# Revit family: NBS_AndersonGECLtd_ShlfUnits_V90ShelvingSystem
name_source: partatom
category: Furniture
revit_build: Autodesk Revit 2017 (Build: 20160225_1515(x64)
units: mm (PartAtom-declared; Revit-internal decimal feet)

## family parameters
Cut with Voids When Loaded = No
Host = Face
Room Calculation Point = No
Shared = No

## types (28) — shared parameters
AssetType = Fixed
Brackets = 170, 270, 370, 470, 570 mm
Category = Pr_40_30_78_77:Shelf units
Default Elevation = 1000 mm  [stored 3.28084 ft]
Description = A wall-fixed 3-part stainless steel system
DimensionsShelfSpacing = 400, 600, 800, 1000, 1500, 1800, 2000 mm
DurationUnit = year
ExpectedLife = 30 years
Features = Components available individually can can be configured as required, shelves , are solid, components can be used in combination with other materials
Finish = Brushed satin stainless steel
Form = Wall mounted single sided unit
IfcExportAs = IfcFurnitureType
IfcExportType = SHELVING
IntegralAccessories = Perforated shelves, barred shelf
IsBuiltIn = Yes
IsMultipleShelves = Yes
IsSingleShelf = No
ManufacturerName = Anderson, GEC Ltd
ManufacturerURL = www.gecanderson.co.uk
Material = Stainless steel
ModelNumber = V90
ModelReference = Shelf Units
NBSCertification = www.nationalbimlibrary.com/cert/lzvmrkqh
NBSDescription = Shelf units
NBSReference = 45-35-80/310
Name = ShelfUnits_V90ShelvingSystem_AndersonGECLtd
NominalLength = 1000 mm  [stored 3.28084 ft]
ProductInformation = http://www.gecanderson.co.uk
Shape = Rectangle
ShelfBottomOffset = 100 mm  [stored 0.328084 ft]
ShelfLength = 1000 mm  [stored 3.28084 ft]
ShelfMaterial = NBS_Concept
Status = UNSET
Style = Shelving
SupportMaterial = NBS_Concept
Uniclass2015Code = Pr_40_30_78_77
Uniclass2015Title = Shelf units
Uniclass2015Version = Products v1.11
UprightSideOffset = 15 mm  [stored 0.0492126 ft]
UprightSpacing = 970 mm  [stored 3.18241 ft]
UprightsNumber = 2
Version = 1
WarrantyDurationUnit = year
WidthOptions = 200, 300, 400, 500 mm

## per-type parameters (varying)
| type | BIMObjectName | BracketWidth | NominalDepth | NominalHeight | NominalWidth | ShelfHeight | ShelfSpacing | ShelfSpacingCalc | ShelfWidth | ShelvesNumber | ShelvesNumberCalc | Size |
| ShelvingUnit200x400 | NBS_AndersonGECLtd_ShelfUnits_V90ShelvingSystem_200x400 | 170 mm  [stored 0.557743 ft] | 200 mm  [stored 0.656168 ft] | 400 mm  [stored 1.31234 ft] | 200 mm  [stored 0.656168 ft] | 400 mm  [stored 1.31234 ft] | 300 mm | 300 mm | 200 mm  [stored 0.656168 ft] | 2 | 2 | 1000 x 400 x 200 mm |
| ShelvingUnit200x600 | NBS_AndersonGECLtd_ShelfUnits_V90ShelvingSystem_200x600 | 170 mm  [stored 0.557743 ft] | 200 mm  [stored 0.656168 ft] | 600 mm | 200 mm  [stored 0.656168 ft] | 600 mm | 250 mm | 250 mm | 200 mm  [stored 0.656168 ft] | 3 | 3 | 1000 x 600 x 200 mm |
| ShelvingUnit200x800 | NBS_AndersonGECLtd_ShelfUnits_V90ShelvingSystem_200x800 | 170 mm  [stored 0.557743 ft] | 200 mm  [stored 0.656168 ft] | 800 mm | 200 mm  [stored 0.656168 ft] | 800 mm | 350 mm | 350 mm | 200 mm  [stored 0.656168 ft] | 3 | 3 | 1000 x 800 x 200 mm |
| ShelvingUnit200x1000 | NBS_AndersonGECLtd_ShelfUnits_V90ShelvingSystem_200x1000 | 170 mm  [stored 0.557743 ft] | 200 mm  [stored 0.656168 ft] | 1000 mm  [stored 3.28084 ft] | 200 mm  [stored 0.656168 ft] | 1000 mm  [stored 3.28084 ft] | 300 mm | 300 mm | 200 mm  [stored 0.656168 ft] | 4 | 4 | 1000 x 1000 x 200 mm |
| ShelvingUnit200x1500 | NBS_AndersonGECLtd_ShelfUnits_V90ShelvingSystem_200x1500 | 170 mm  [stored 0.557743 ft] | 200 mm  [stored 0.656168 ft] | 1500 mm | 200 mm  [stored 0.656168 ft] | 1500 mm | 280 mm | 280 mm | 200 mm  [stored 0.656168 ft] | 6 | 6 | 1000 x 1500 x 200 mm |
| ShelvingUnit200x1800 | NBS_AndersonGECLtd_ShelfUnits_V90ShelvingSystem_200x1800 | 170 mm  [stored 0.557743 ft] | 200 mm  [stored 0.656168 ft] | 1800 mm | 200 mm  [stored 0.656168 ft] | 1800 mm | 280 mm | 280 mm | 200 mm  [stored 0.656168 ft] | 7 | 7 | 1000 x 1800 x 200 mm |
| ShelvingUnit200x2000 | NBS_AndersonGECLtd_ShelfUnits_V90ShelvingSystem_200x2000 | 170 mm  [stored 0.557743 ft] | 200 mm  [stored 0.656168 ft] | 2000 mm  [stored 6.56168 ft] | 200 mm  [stored 0.656168 ft] | 2000 mm  [stored 6.56168 ft] | 270 mm | 270 mm | 200 mm  [stored 0.656168 ft] | 8 | 8 | 1000 x 2000 x 200 mm |
| ShelvingUnit300x400 | NBS_AndersonGECLtd_ShelfUnits_V90ShelvingSystem_300x400 | 270 mm | 300 mm | 400 mm  [stored 1.31234 ft] | 300 mm | 400 mm  [stored 1.31234 ft] | 300 mm | 300 mm | 300 mm | 2 | 2 | 1000 x 400 x 200 mm |
| ShelvingUnit300x600 | NBS_AndersonGECLtd_ShelfUnits_V90ShelvingSystem_300x600 | 270 mm | 300 mm | 600 mm | 300 mm | 600 mm | 250 mm | 250 mm | 300 mm | 3 | 3 | 1000 x 600 x 300 mm |
| ShelvingUnit300x800 | NBS_AndersonGECLtd_ShelfUnits_V90ShelvingSystem_300x800 | 270 mm | 300 mm | 800 mm | 300 mm | 800 mm | 350 mm | 350 mm | 300 mm | 3 | 3 | 1000 x 800 x 300 mm |
| ShelvingUnit300x1000 | NBS_AndersonGECLtd_ShelfUnits_V90ShelvingSystem_300x1000 | 270 mm | 300 mm | 1000 mm  [stored 3.28084 ft] | 300 mm | 1000 mm  [stored 3.28084 ft] | 300 mm | 300 mm | 300 mm | 4 | 4 | 1000 x 1000 x 300 mm |
| ShelvingUnit300x1500 | NBS_AndersonGECLtd_ShelfUnits_V90ShelvingSystem_300x1500 | 270 mm | 300 mm | 1500 mm | 300 mm | 1500 mm | 280 mm | 280 mm | 300 mm | 6 | 6 | 1000 x 1500 x 300 mm |
| ShelvingUnit300x1800 | NBS_AndersonGECLtd_ShelfUnits_V90ShelvingSystem_300x1800 | 270 mm | 300 mm | 1800 mm | 300 mm | 1800 mm | 280 mm | 280 mm | 300 mm | 7 | 7 | 1000 x 1800 x 300 mm |
| ShelvingUnit300x2000 | NBS_AndersonGECLtd_ShelfUnits_V90ShelvingSystem_300x1800 | 270 mm | 300 mm | 2000 mm  [stored 6.56168 ft] | 300 mm | 2000 mm  [stored 6.56168 ft] | 270 mm | 270 mm | 300 mm | 8 | 8 | 1000 x 2000 x 300 mm |
| ShelvingUnit400x400 | NBS_AndersonGECLtd_ShelfUnits_V90ShelvingSystem_400x400 | 370 mm | 400 mm  [stored 1.31234 ft] | 400 mm  [stored 1.31234 ft] | 400 mm  [stored 1.31234 ft] | 400 mm  [stored 1.31234 ft] | 300 mm | 300 mm | 400 mm  [stored 1.31234 ft] | 2 | 2 | 1000 x 400 x 400 mm |
| ShelvingUnit400x600 | NBS_AndersonGECLtd_ShelfUnits_V90ShelvingSystem_400x600 | 370 mm | 400 mm  [stored 1.31234 ft] | 600 mm | 400 mm  [stored 1.31234 ft] | 600 mm | 250 mm | 250 mm | 400 mm  [stored 1.31234 ft] | 3 | 3 | 1000 x 600 x 400 mm |
| ShelvingUnit400x800 | NBS_AndersonGECLtd_ShelfUnits_V90ShelvingSystem_400x800 | 370 mm | 400 mm  [stored 1.31234 ft] | 800 mm | 400 mm  [stored 1.31234 ft] | 800 mm | 350 mm | 350 mm | 400 mm  [stored 1.31234 ft] | 3 | 3 | 1000 x 800 x 400 mm |
| ShelvingUnit400x1000 | NBS_AndersonGECLtd_ShelfUnits_V90ShelvingSystem_400x1000 | 370 mm | 400 mm  [stored 1.31234 ft] | 1000 mm  [stored 3.28084 ft] | 400 mm  [stored 1.31234 ft] | 1000 mm  [stored 3.28084 ft] | 300 mm | 300 mm | 400 mm  [stored 1.31234 ft] | 4 | 4 | 1000 x 1000 x 400 mm |
| ShelvingUnit400x1500 | NBS_AndersonGECLtd_ShelfUnits_V90ShelvingSystem_400x1500 | 370 mm | 400 mm  [stored 1.31234 ft] | 1500 mm | 400 mm  [stored 1.31234 ft] | 1500 mm | 280 mm | 280 mm | 400 mm  [stored 1.31234 ft] | 6 | 6 | 1000 x 1500 x 400 mm |
| ShelvingUnit400x1800 | NBS_AndersonGECLtd_ShelfUnits_V90ShelvingSystem_400x1800 | 370 mm | 400 mm  [stored 1.31234 ft] | 1800 mm | 400 mm  [stored 1.31234 ft] | 1800 mm | 280 mm | 280 mm | 400 mm  [stored 1.31234 ft] | 7 | 7 | 1000 x 1800 x 400 mm |
| ShelvingUnit400x2000 | NBS_AndersonGECLtd_ShelfUnits_V90ShelvingSystem_400x2000 | 370 mm | 400 mm  [stored 1.31234 ft] | 2000 mm  [stored 6.56168 ft] | 400 mm  [stored 1.31234 ft] | 2000 mm  [stored 6.56168 ft] | 270 mm | 270 mm | 400 mm  [stored 1.31234 ft] | 8 | 8 | 1000 x 2000 x 400 mm |
| ShelvingUnit500x400 | NBS_AndersonGECLtd_ShelfUnits_V90ShelvingSystem_500x400 | 470 mm | 500 mm  [stored 1.64042 ft] | 400 mm  [stored 1.31234 ft] | 500 mm  [stored 1.64042 ft] | 400 mm  [stored 1.31234 ft] | 300 mm | 300 mm | 500 mm  [stored 1.64042 ft] | 2 | 2 | 1000 x 400 x 500 mm |
| ShelvingUnit500x600 | NBS_AndersonGECLtd_ShelfUnits_V90ShelvingSystem_500x600 | 470 mm | 500 mm  [stored 1.64042 ft] | 600 mm | 500 mm  [stored 1.64042 ft] | 600 mm | 250 mm | 250 mm | 500 mm  [stored 1.64042 ft] | 3 | 3 | 1000 x 600 x 500 mm |
| ShelvingUnit500x800 | NBS_AndersonGECLtd_ShelfUnits_V90ShelvingSystem_500x800 | 470 mm | 500 mm  [stored 1.64042 ft] | 800 mm | 500 mm  [stored 1.64042 ft] | 800 mm | 350 mm | 350 mm | 500 mm  [stored 1.64042 ft] | 3 | 3 | 1000 x 800 x 500 mm |
| ShelvingUnit500x1000 | NBS_AndersonGECLtd_ShelfUnits_V90ShelvingSystem_500x1000 | 470 mm | 500 mm  [stored 1.64042 ft] | 1000 mm  [stored 3.28084 ft] | 500 mm  [stored 1.64042 ft] | 1000 mm  [stored 3.28084 ft] | 300 mm | 300 mm | 500 mm  [stored 1.64042 ft] | 4 | 4 | 1000 x 1000 x 500 mm |
| ShelvingUnit500x1500 | NBS_AndersonGECLtd_ShelfUnits_V90ShelvingSystem_500x1500 | 470 mm | 500 mm  [stored 1.64042 ft] | 1500 mm | 500 mm  [stored 1.64042 ft] | 1500 mm | 280 mm | 280 mm | 500 mm  [stored 1.64042 ft] | 6 | 6 | 1000 x 1500 x 500 mm |
| ShelvingUnit500x1800 | NBS_AndersonGECLtd_ShelfUnits_V90ShelvingSystem_500x1800 | 470 mm | 500 mm  [stored 1.64042 ft] | 1800 mm | 500 mm  [stored 1.64042 ft] | 1800 mm | 280 mm | 280 mm | 500 mm  [stored 1.64042 ft] | 7 | 7 | 1000 x 1800 x 500 mm |
| ShelvingUnit500x2000 | NBS_AndersonGECLtd_ShelfUnits_V90ShelvingSystem_500x2000 | 470 mm | 500 mm  [stored 1.64042 ft] | 2000 mm  [stored 6.56168 ft] | 500 mm  [stored 1.64042 ft] | 2000 mm  [stored 6.56168 ft] | 270 mm | 270 mm | 500 mm  [stored 1.64042 ft] | 8 | 8 | 1000 x 2000 x 500 mm |

note: [stored X ft] marks values corroborated as IEEE doubles in the binary element streams (Revit-internal decimal feet)

## geometry (parser evidence)
native form markers: Sweep x10
no freeform markers — native parametric forms only
